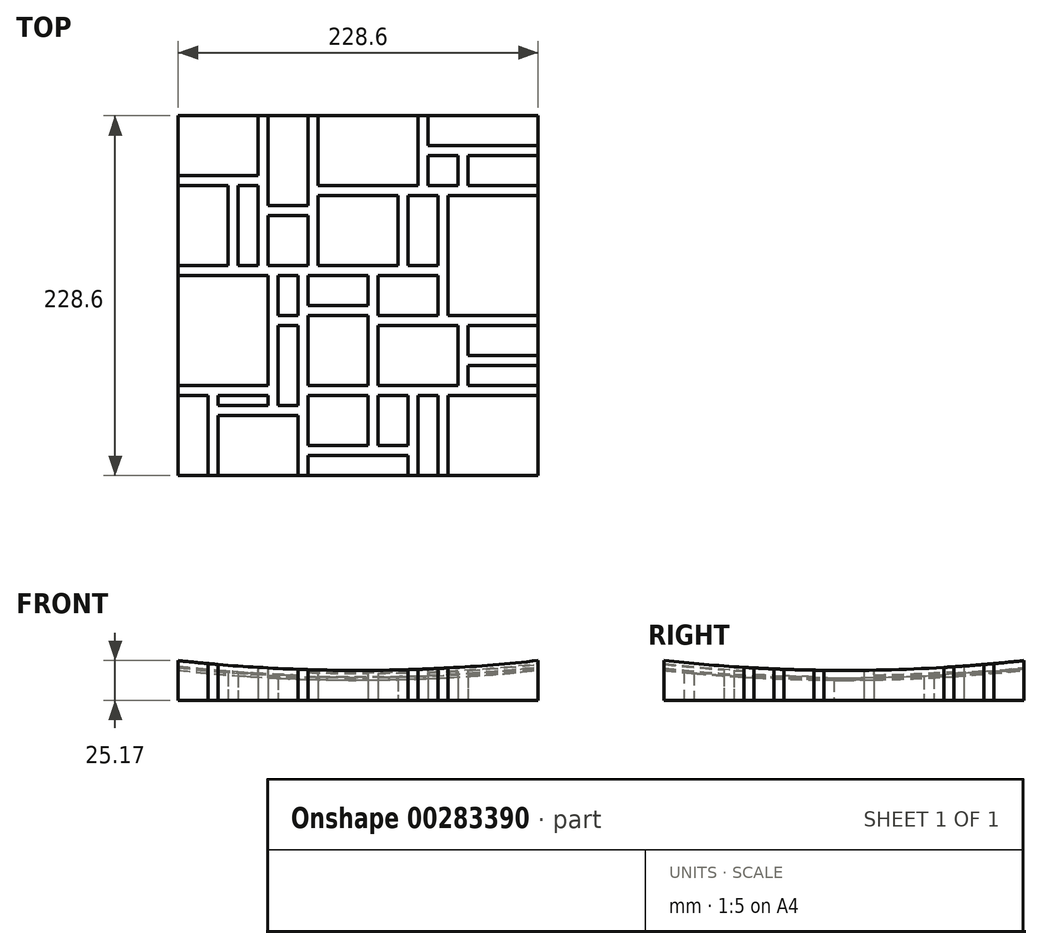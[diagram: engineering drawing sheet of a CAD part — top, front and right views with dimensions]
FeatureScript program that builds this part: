
annotation { "Feature Type Name" : "Feature", "Feature Type Description" : "" }
export const myFeature = defineFeature(function(context is Context, id is Id, definition is map)
    precondition{}
    {
        {
            var Q0;
            Q0=qCreatedBy(makeId("Top.planeOp"),FACE);
            var sketch = newSketch(context, id + "F0", { "sketchPlane" : qUnion([Q0])});
            skLineSegment(sketch, "E0.bottom", {"start": v(114.3, -114.3) * mm, "end": v(-114.3, -114.3) * mm});
            skLineSegment(sketch, "E0.top", {"start": v(114.3, 114.3) * mm, "end": v(-114.3, 114.3) * mm});
            skLineSegment(sketch, "E0.left", {"start": v(114.3, -114.3) * mm, "end": v(114.3, 114.3) * mm});
            skLineSegment(sketch, "E0.right", {"start": v(-114.3, -114.3) * mm, "end": v(-114.3, 114.3) * mm});
            skPoint(sketch, "E0.middle", {"position": v(0, 0) * mm});
            skLineSegment(sketch, "E1", {"start": v(-114.3, 114.3) * mm, "end": v(-63.5, 114.3) * mm, "construction": true});
            skLineSegment(sketch, "E2", {"start": v(-63.5, 114.3) * mm, "end": v(-63.5, 76.2) * mm});
            skLineSegment(sketch, "E3", {"start": v(-63.5, 76.2) * mm, "end": v(-114.3, 76.2) * mm});
            skLineSegment(sketch, "E4", {"start": v(-114.3, 76.2) * mm, "end": v(-114.3, 69.85) * mm, "construction": true});
            skLineSegment(sketch, "E5", {"start": v(-114.3, 69.85) * mm, "end": v(-114.3, 19.05) * mm, "construction": true});
            skLineSegment(sketch, "E6", {"start": v(-114.3, 19.05) * mm, "end": v(-82.55, 19.05) * mm});
            skLineSegment(sketch, "E7", {"start": v(-82.55, 19.05) * mm, "end": v(-82.55, 69.85) * mm});
            skLineSegment(sketch, "E8", {"start": v(-82.55, 69.85) * mm, "end": v(-114.3, 69.85) * mm});
            skLineSegment(sketch, "E9", {"start": v(-82.55, 69.85) * mm, "end": v(-76.2, 69.85) * mm, "construction": true});
            skLineSegment(sketch, "E10", {"start": v(-76.2, 69.85) * mm, "end": v(-63.5, 69.85) * mm});
            skLineSegment(sketch, "E11", {"start": v(-63.5, 69.85) * mm, "end": v(-63.5, 19.05) * mm});
            skLineSegment(sketch, "E12", {"start": v(-63.5, 19.05) * mm, "end": v(-76.2, 19.05) * mm});
            skLineSegment(sketch, "E13", {"start": v(-76.2, 19.05) * mm, "end": v(-76.2, 69.85) * mm});
            skLineSegment(sketch, "E14", {"start": v(-63.5, 114.3) * mm, "end": v(-57.15, 114.3) * mm, "construction": true});
            skLineSegment(sketch, "E15", {"start": v(-57.15, 114.3) * mm, "end": v(-57.15, 57.15) * mm});
            skLineSegment(sketch, "E16", {"start": v(-57.15, 57.15) * mm, "end": v(-31.75, 57.15) * mm});
            skLineSegment(sketch, "E17", {"start": v(-31.75, 57.15) * mm, "end": v(-31.75, 114.3) * mm});
            skLineSegment(sketch, "E18", {"start": v(-31.75, 114.3) * mm, "end": v(-25.4, 114.3) * mm, "construction": true});
            skLineSegment(sketch, "E19", {"start": v(-25.4, 114.3) * mm, "end": v(-25.4, 69.85) * mm});
            skLineSegment(sketch, "E20", {"start": v(-25.4, 69.85) * mm, "end": v(38.1, 69.85) * mm});
            skLineSegment(sketch, "E21", {"start": v(38.1, 69.85) * mm, "end": v(38.1, 114.3) * mm});
            skLineSegment(sketch, "E22", {"start": v(38.1, 114.3) * mm, "end": v(44.45, 114.3) * mm, "construction": true});
            skLineSegment(sketch, "E23", {"start": v(44.45, 114.3) * mm, "end": v(44.45, 95.25) * mm});
            skLineSegment(sketch, "E24", {"start": v(44.45, 95.25) * mm, "end": v(114.3, 95.25) * mm});
            skLineSegment(sketch, "E25", {"start": v(114.3, 95.25) * mm, "end": v(114.3, 88.9) * mm, "construction": true});
            skLineSegment(sketch, "E26", {"start": v(114.3, 88.9) * mm, "end": v(69.85, 88.9) * mm});
            skLineSegment(sketch, "E27", {"start": v(69.85, 88.9) * mm, "end": v(69.85, 69.85) * mm});
            skLineSegment(sketch, "E28", {"start": v(69.85, 69.85) * mm, "end": v(114.3, 69.85) * mm});
            skLineSegment(sketch, "E29", {"start": v(69.85, 88.9) * mm, "end": v(63.5, 88.9) * mm, "construction": true});
            skLineSegment(sketch, "E30", {"start": v(63.5, 88.9) * mm, "end": v(44.45, 88.9) * mm});
            skLineSegment(sketch, "E31", {"start": v(44.45, 88.9) * mm, "end": v(44.45, 69.85) * mm});
            skLineSegment(sketch, "E32", {"start": v(44.45, 69.85) * mm, "end": v(63.5, 69.85) * mm});
            skLineSegment(sketch, "E33", {"start": v(63.5, 69.85) * mm, "end": v(63.5, 88.9) * mm});
            skLineSegment(sketch, "E34", {"start": v(114.3, 69.85) * mm, "end": v(114.3, 63.5) * mm, "construction": true});
            skLineSegment(sketch, "E35", {"start": v(114.3, 63.5) * mm, "end": v(57.15, 63.5) * mm});
            skLineSegment(sketch, "E36", {"start": v(57.15, 63.5) * mm, "end": v(57.15, -12.7) * mm});
            skLineSegment(sketch, "E37", {"start": v(57.15, -12.7) * mm, "end": v(114.3, -12.7) * mm});
            skLineSegment(sketch, "E38", {"start": v(114.3, -12.7) * mm, "end": v(114.3, -19.05) * mm, "construction": true});
            skLineSegment(sketch, "E39", {"start": v(114.3, -19.05) * mm, "end": v(69.85, -19.05) * mm});
            skLineSegment(sketch, "E40", {"start": v(69.85, -19.05) * mm, "end": v(69.85, -38.1) * mm});
            skLineSegment(sketch, "E41", {"start": v(69.85, -38.1) * mm, "end": v(114.3, -38.1) * mm});
            skLineSegment(sketch, "E42", {"start": v(114.3, -38.1) * mm, "end": v(114.3, -44.45) * mm, "construction": true});
            skLineSegment(sketch, "E43", {"start": v(114.3, -44.45) * mm, "end": v(69.85, -44.45) * mm});
            skLineSegment(sketch, "E44", {"start": v(69.85, -44.45) * mm, "end": v(69.85, -57.15) * mm});
            skLineSegment(sketch, "E45", {"start": v(69.85, -57.15) * mm, "end": v(114.3, -57.15) * mm});
            skLineSegment(sketch, "E46", {"start": v(114.3, -57.15) * mm, "end": v(114.3, -63.5) * mm, "construction": true});
            skLineSegment(sketch, "E47", {"start": v(114.3, -63.5) * mm, "end": v(57.15, -63.5) * mm});
            skLineSegment(sketch, "E48", {"start": v(57.15, -63.5) * mm, "end": v(57.15, -114.3) * mm});
            skLineSegment(sketch, "E49", {"start": v(57.15, -114.3) * mm, "end": v(50.8, -114.3) * mm, "construction": true});
            skLineSegment(sketch, "E50", {"start": v(50.8, -114.3) * mm, "end": v(50.8, -63.5) * mm});
            skLineSegment(sketch, "E51", {"start": v(50.8, -63.5) * mm, "end": v(38.1, -63.5) * mm});
            skLineSegment(sketch, "E52", {"start": v(38.1, -63.5) * mm, "end": v(38.1, -114.3) * mm});
            skLineSegment(sketch, "E53", {"start": v(38.1, -114.3) * mm, "end": v(31.75, -114.3) * mm, "construction": true});
            skLineSegment(sketch, "E54", {"start": v(31.75, -114.3) * mm, "end": v(31.75, -101.6) * mm});
            skLineSegment(sketch, "E55", {"start": v(31.75, -101.6) * mm, "end": v(-31.75, -101.6) * mm});
            skLineSegment(sketch, "E56", {"start": v(-31.75, -101.6) * mm, "end": v(-31.75, -114.3) * mm});
            skLineSegment(sketch, "E57", {"start": v(31.75, -101.6) * mm, "end": v(31.75, -95.25) * mm, "construction": true});
            skLineSegment(sketch, "E58", {"start": v(31.75, -95.25) * mm, "end": v(31.75, -63.5) * mm});
            skLineSegment(sketch, "E59", {"start": v(31.75, -63.5) * mm, "end": v(12.7, -63.5) * mm});
            skLineSegment(sketch, "E60", {"start": v(12.7, -63.5) * mm, "end": v(12.7, -95.25) * mm});
            skLineSegment(sketch, "E61", {"start": v(12.7, -95.25) * mm, "end": v(31.75, -95.25) * mm});
            skLineSegment(sketch, "E62", {"start": v(12.7, -63.5) * mm, "end": v(6.35, -63.5) * mm, "construction": true});
            skLineSegment(sketch, "E63", {"start": v(6.35, -63.5) * mm, "end": v(-31.75, -63.5) * mm});
            skLineSegment(sketch, "E64", {"start": v(-31.75, -63.5) * mm, "end": v(-31.75, -95.25) * mm});
            skLineSegment(sketch, "E65", {"start": v(-31.75, -95.25) * mm, "end": v(6.35, -95.25) * mm});
            skLineSegment(sketch, "E66", {"start": v(6.35, -95.25) * mm, "end": v(6.35, -63.5) * mm});
            skLineSegment(sketch, "E67", {"start": v(12.7, -63.5) * mm, "end": v(12.7, -57.15) * mm, "construction": true});
            skLineSegment(sketch, "E68", {"start": v(12.7, -57.15) * mm, "end": v(63.5, -57.15) * mm});
            skLineSegment(sketch, "E69", {"start": v(63.5, -57.15) * mm, "end": v(63.5, -19.05) * mm});
            skLineSegment(sketch, "E70", {"start": v(63.5, -19.05) * mm, "end": v(12.7, -19.05) * mm});
            skLineSegment(sketch, "E71", {"start": v(12.7, -19.05) * mm, "end": v(12.7, -57.15) * mm});
            skLineSegment(sketch, "E72", {"start": v(-31.75, -114.3) * mm, "end": v(-38.1, -114.3) * mm, "construction": true});
            skLineSegment(sketch, "E73", {"start": v(-38.1, -114.3) * mm, "end": v(-38.1, -76.2) * mm});
            skLineSegment(sketch, "E74", {"start": v(-38.1, -76.2) * mm, "end": v(-88.9, -76.2) * mm});
            skLineSegment(sketch, "E75", {"start": v(-88.9, -76.2) * mm, "end": v(-88.9, -114.3) * mm});
            skLineSegment(sketch, "E76", {"start": v(-88.9, -114.3) * mm, "end": v(-95.25, -114.3) * mm, "construction": true});
            skLineSegment(sketch, "E77", {"start": v(-95.25, -114.3) * mm, "end": v(-95.25, -63.5) * mm});
            skLineSegment(sketch, "E78", {"start": v(-95.25, -63.5) * mm, "end": v(-114.3, -63.5) * mm});
            skLineSegment(sketch, "E79", {"start": v(-114.3, -63.5) * mm, "end": v(-114.3, -57.15) * mm, "construction": true});
            skLineSegment(sketch, "E80", {"start": v(-114.3, -57.15) * mm, "end": v(-57.15, -57.15) * mm});
            skLineSegment(sketch, "E81", {"start": v(-57.15, -57.15) * mm, "end": v(-57.15, 12.7) * mm});
            skLineSegment(sketch, "E82", {"start": v(-57.15, 12.7) * mm, "end": v(-114.3, 12.7) * mm});
            skLineSegment(sketch, "E83", {"start": v(-88.9, -76.2) * mm, "end": v(-88.9, -69.85) * mm, "construction": true});
            skLineSegment(sketch, "E84", {"start": v(-88.9, -69.85) * mm, "end": v(-88.9, -63.5) * mm});
            skLineSegment(sketch, "E85", {"start": v(-88.9, -63.5) * mm, "end": v(-57.15, -63.5) * mm});
            skLineSegment(sketch, "E86", {"start": v(-57.15, -63.5) * mm, "end": v(-57.15, -69.85) * mm});
            skLineSegment(sketch, "E87", {"start": v(-57.15, -69.85) * mm, "end": v(-88.9, -69.85) * mm});
            skLineSegment(sketch, "E88", {"start": v(-38.1, -76.2) * mm, "end": v(-38.1, -69.85) * mm, "construction": true});
            skLineSegment(sketch, "E89", {"start": v(-38.1, -69.85) * mm, "end": v(-50.8, -69.85) * mm});
            skLineSegment(sketch, "E90", {"start": v(-50.8, -69.85) * mm, "end": v(-50.8, -19.05) * mm});
            skLineSegment(sketch, "E91", {"start": v(-50.8, -19.05) * mm, "end": v(-38.1, -19.05) * mm});
            skLineSegment(sketch, "E92", {"start": v(-38.1, -19.05) * mm, "end": v(-38.1, -69.85) * mm});
            skLineSegment(sketch, "E93", {"start": v(-63.5, 19.05) * mm, "end": v(-57.15, 19.05) * mm, "construction": true});
            skLineSegment(sketch, "E94", {"start": v(-57.15, 19.05) * mm, "end": v(-57.15, 50.8) * mm});
            skLineSegment(sketch, "E95", {"start": v(-57.15, 50.8) * mm, "end": v(-31.75, 50.8) * mm});
            skLineSegment(sketch, "E96", {"start": v(-31.75, 50.8) * mm, "end": v(-31.75, 19.05) * mm});
            skLineSegment(sketch, "E97", {"start": v(-31.75, 19.05) * mm, "end": v(-57.15, 19.05) * mm});
            skLineSegment(sketch, "E98", {"start": v(-38.1, -19.05) * mm, "end": v(-38.1, -12.7) * mm, "construction": true});
            skLineSegment(sketch, "E99", {"start": v(-38.1, -12.7) * mm, "end": v(-50.8, -12.7) * mm});
            skLineSegment(sketch, "E100", {"start": v(-50.8, -12.7) * mm, "end": v(-50.8, 12.7) * mm});
            skLineSegment(sketch, "E101", {"start": v(-50.8, 12.7) * mm, "end": v(-38.1, 12.7) * mm});
            skLineSegment(sketch, "E102", {"start": v(-38.1, 12.7) * mm, "end": v(-38.1, -12.7) * mm});
            skLineSegment(sketch, "E103", {"start": v(-31.75, -63.5) * mm, "end": v(-31.75, -57.15) * mm, "construction": true});
            skLineSegment(sketch, "E104", {"start": v(-31.75, -57.15) * mm, "end": v(-31.75, -12.7) * mm});
            skLineSegment(sketch, "E105", {"start": v(-31.75, -12.7) * mm, "end": v(6.35, -12.7) * mm});
            skLineSegment(sketch, "E106", {"start": v(6.35, -12.7) * mm, "end": v(6.35, -57.15) * mm});
            skLineSegment(sketch, "E107", {"start": v(6.35, -57.15) * mm, "end": v(-31.75, -57.15) * mm});
            skLineSegment(sketch, "E108", {"start": v(-31.75, 19.05) * mm, "end": v(-31.75, 12.7) * mm, "construction": true});
            skLineSegment(sketch, "E109", {"start": v(-31.75, 12.7) * mm, "end": v(-31.75, -6.35) * mm});
            skLineSegment(sketch, "E110", {"start": v(-31.75, -6.35) * mm, "end": v(6.35, -6.35) * mm});
            skLineSegment(sketch, "E111", {"start": v(6.35, -6.35) * mm, "end": v(6.35, 12.7) * mm});
            skLineSegment(sketch, "E112", {"start": v(6.35, 12.7) * mm, "end": v(-31.75, 12.7) * mm});
            skLineSegment(sketch, "E113", {"start": v(-25.4, 69.85) * mm, "end": v(-25.4, 63.5) * mm, "construction": true});
            skLineSegment(sketch, "E114", {"start": v(-25.4, 63.5) * mm, "end": v(-25.4, 19.05) * mm});
            skLineSegment(sketch, "E115", {"start": v(-25.4, 19.05) * mm, "end": v(25.4, 19.05) * mm});
            skLineSegment(sketch, "E116", {"start": v(25.4, 19.05) * mm, "end": v(25.4, 63.5) * mm});
            skLineSegment(sketch, "E117", {"start": v(25.4, 63.5) * mm, "end": v(-25.4, 63.5) * mm});
            skLineSegment(sketch, "E118", {"start": v(25.4, 63.5) * mm, "end": v(31.75, 63.5) * mm, "construction": true});
            skLineSegment(sketch, "E119", {"start": v(31.75, 63.5) * mm, "end": v(31.75, 19.05) * mm});
            skLineSegment(sketch, "E120", {"start": v(31.75, 19.05) * mm, "end": v(50.8, 19.05) * mm});
            skLineSegment(sketch, "E121", {"start": v(50.8, 19.05) * mm, "end": v(50.8, 63.5) * mm});
            skLineSegment(sketch, "E122", {"start": v(50.8, 63.5) * mm, "end": v(31.75, 63.5) * mm});
            skLineSegment(sketch, "E123", {"start": v(50.8, 19.05) * mm, "end": v(50.8, 12.7) * mm, "construction": true});
            skLineSegment(sketch, "E124", {"start": v(50.8, 12.7) * mm, "end": v(12.7, 12.7) * mm});
            skLineSegment(sketch, "E125", {"start": v(12.7, 12.7) * mm, "end": v(12.7, -12.7) * mm});
            skLineSegment(sketch, "E126", {"start": v(12.7, -12.7) * mm, "end": v(50.8, -12.7) * mm});
            skLineSegment(sketch, "E127", {"start": v(50.8, -12.7) * mm, "end": v(50.8, 12.7) * mm});
            skSolve(sketch);
        }
        {
            var Q0;
            {var subQ15=sQuery(id+"F0.wireOp",EDGE,"E2");Q0=makeQuery(id+"F0.imprint","IMPRINT",FACE,{"disambiguationData":[TD([[makeQuery(id+"F0.imprint","IMPRINT",EDGE,{"derivedFrom":subQ15}),1.0]])]});}
            extrude(context, id + "F1", {"entities" : qUnion([Q0]), "depth" : 25.4 * mm});
        }
        {
            var Q0;
            {var subQ0=sQuery(id+"F0.wireOp",EDGE,"E73");Q0=makeQuery(id+"F0.imprint","IMPRINT",FACE,{"disambiguationData":[TD([[makeQuery(id+"F0.imprint","IMPRINT",EDGE,{"derivedFrom":subQ0}),1.0]])]});}
            var Q1;
            Q1=makeQuery(id+"F0.imprint","IMPRINT",FACE,{"disambiguationData":[TD([[makeQuery(id+"F0.imprint","IMPRINT",EDGE,{"derivedFrom":sQuery(id+"F0.wireOp",EDGE,"E114")}),1.0]])]});
            var Q2;
            Q2=makeQuery(id+"F0.imprint","IMPRINT",FACE,{"disambiguationData":[TD([[makeQuery(id+"F0.imprint","IMPRINT",EDGE,{"derivedFrom":sQuery(id+"F0.wireOp",EDGE,"E68")}),1.0]])]});
            var Q3;
            {var subQ0=sQuery(id+"F0.wireOp",EDGE,"E80");Q3=makeQuery(id+"F0.imprint","IMPRINT",FACE,{"disambiguationData":[TD([[makeQuery(id+"F0.imprint","IMPRINT",EDGE,{"derivedFrom":subQ0}),1.0]])]});}
            var Q4;
            Q4=makeQuery(id+"F0.imprint","IMPRINT",FACE,{"disambiguationData":[TD([[makeQuery(id+"F0.imprint","IMPRINT",EDGE,{"derivedFrom":sQuery(id+"F0.wireOp",EDGE,"E89")}),-1.0]])]});
            var Q5;
            Q5=makeQuery(id+"F0.imprint","IMPRINT",FACE,{"disambiguationData":[TD([[makeQuery(id+"F0.imprint","IMPRINT",EDGE,{"derivedFrom":sQuery(id+"F0.wireOp",EDGE,"E84")}),-1.0]])]});
            var Q6;
            {var subQ3=sQuery(id+"F0.wireOp",EDGE,"E77");Q6=makeQuery(id+"F0.imprint","IMPRINT",FACE,{"disambiguationData":[TD([[makeQuery(id+"F0.imprint","IMPRINT",EDGE,{"derivedFrom":subQ3}),1.0]])]});}
            var Q7;
            Q7=makeQuery(id+"F0.imprint","IMPRINT",FACE,{"disambiguationData":[TD([[makeQuery(id+"F0.imprint","IMPRINT",EDGE,{"derivedFrom":sQuery(id+"F0.wireOp",EDGE,"E63")}),1.0]])]});
            var Q8;
            Q8=makeQuery(id+"F0.imprint","IMPRINT",FACE,{"disambiguationData":[TD([[makeQuery(id+"F0.imprint","IMPRINT",EDGE,{"derivedFrom":sQuery(id+"F0.wireOp",EDGE,"E104")}),-1.0]])]});
            var Q9;
            {var subQ0=sQuery(id+"F0.wireOp",EDGE,"E54");Q9=makeQuery(id+"F0.imprint","IMPRINT",FACE,{"disambiguationData":[TD([[makeQuery(id+"F0.imprint","IMPRINT",EDGE,{"derivedFrom":subQ0}),1.0]])]});}
            var Q10;
            Q10=makeQuery(id+"F0.imprint","IMPRINT",FACE,{"disambiguationData":[TD([[makeQuery(id+"F0.imprint","IMPRINT",EDGE,{"derivedFrom":sQuery(id+"F0.wireOp",EDGE,"E58")}),1.0]])]});
            var Q11;
            {var subQ0=sQuery(id+"F0.wireOp",EDGE,"E50");Q11=makeQuery(id+"F0.imprint","IMPRINT",FACE,{"disambiguationData":[TD([[makeQuery(id+"F0.imprint","IMPRINT",EDGE,{"derivedFrom":subQ0}),1.0]])]});}
            var Q12;
            {var subQ4=sQuery(id+"F0.wireOp",EDGE,"E47");Q12=makeQuery(id+"F0.imprint","IMPRINT",FACE,{"disambiguationData":[TD([[makeQuery(id+"F0.imprint","IMPRINT",EDGE,{"derivedFrom":subQ4}),1.0]])]});}
            var Q13;
            {var subQ0=sQuery(id+"F0.wireOp",EDGE,"E43");Q13=makeQuery(id+"F0.imprint","IMPRINT",FACE,{"disambiguationData":[TD([[makeQuery(id+"F0.imprint","IMPRINT",EDGE,{"derivedFrom":subQ0}),1.0]])]});}
            var Q14;
            {var subQ0=sQuery(id+"F0.wireOp",EDGE,"E39");Q14=makeQuery(id+"F0.imprint","IMPRINT",FACE,{"disambiguationData":[TD([[makeQuery(id+"F0.imprint","IMPRINT",EDGE,{"derivedFrom":subQ0}),1.0]])]});}
            var Q15;
            {var subQ0=sQuery(id+"F0.wireOp",EDGE,"E35");Q15=makeQuery(id+"F0.imprint","IMPRINT",FACE,{"disambiguationData":[TD([[makeQuery(id+"F0.imprint","IMPRINT",EDGE,{"derivedFrom":subQ0}),1.0]])]});}
            var Q16;
            {var subQ0=sQuery(id+"F0.wireOp",EDGE,"E26");Q16=makeQuery(id+"F0.imprint","IMPRINT",FACE,{"disambiguationData":[TD([[makeQuery(id+"F0.imprint","IMPRINT",EDGE,{"derivedFrom":subQ0}),1.0]])]});}
            var Q17;
            Q17=makeQuery(id+"F0.imprint","IMPRINT",FACE,{"disambiguationData":[TD([[makeQuery(id+"F0.imprint","IMPRINT",EDGE,{"derivedFrom":sQuery(id+"F0.wireOp",EDGE,"E30")}),1.0]])]});
            var Q18;
            {var subQ3=sQuery(id+"F0.wireOp",EDGE,"E23");Q18=makeQuery(id+"F0.imprint","IMPRINT",FACE,{"disambiguationData":[TD([[makeQuery(id+"F0.imprint","IMPRINT",EDGE,{"derivedFrom":subQ3}),1.0]])]});}
            var Q19;
            {var subQ0=sQuery(id+"F0.wireOp",EDGE,"E19");Q19=makeQuery(id+"F0.imprint","IMPRINT",FACE,{"disambiguationData":[TD([[makeQuery(id+"F0.imprint","IMPRINT",EDGE,{"derivedFrom":subQ0}),1.0]])]});}
            var Q20;
            Q20=makeQuery(id+"F0.imprint","IMPRINT",FACE,{"disambiguationData":[TD([[makeQuery(id+"F0.imprint","IMPRINT",EDGE,{"derivedFrom":sQuery(id+"F0.wireOp",EDGE,"E119")}),1.0]])]});
            var Q21;
            Q21=makeQuery(id+"F0.imprint","IMPRINT",FACE,{"disambiguationData":[TD([[makeQuery(id+"F0.imprint","IMPRINT",EDGE,{"derivedFrom":sQuery(id+"F0.wireOp",EDGE,"E124")}),1.0]])]});
            var Q22;
            Q22=makeQuery(id+"F0.imprint","IMPRINT",FACE,{"disambiguationData":[TD([[makeQuery(id+"F0.imprint","IMPRINT",EDGE,{"derivedFrom":sQuery(id+"F0.wireOp",EDGE,"E109")}),1.0]])]});
            var Q23;
            Q23=makeQuery(id+"F0.imprint","IMPRINT",FACE,{"disambiguationData":[TD([[makeQuery(id+"F0.imprint","IMPRINT",EDGE,{"derivedFrom":sQuery(id+"F0.wireOp",EDGE,"E99")}),-1.0]])]});
            var Q24;
            Q24=makeQuery(id+"F0.imprint","IMPRINT",FACE,{"disambiguationData":[TD([[makeQuery(id+"F0.imprint","IMPRINT",EDGE,{"derivedFrom":sQuery(id+"F0.wireOp",EDGE,"E94")}),-1.0]])]});
            var Q25;
            Q25=makeQuery(id+"F0.imprint","IMPRINT",FACE,{"disambiguationData":[TD([[makeQuery(id+"F0.imprint","IMPRINT",EDGE,{"derivedFrom":sQuery(id+"F0.wireOp",EDGE,"E10")}),-1.0]])]});
            var Q26;
            {var subQ0=sQuery(id+"F0.wireOp",EDGE,"E6");Q26=makeQuery(id+"F0.imprint","IMPRINT",FACE,{"disambiguationData":[TD([[makeQuery(id+"F0.imprint","IMPRINT",EDGE,{"derivedFrom":subQ0}),1.0]])]});}
            var Q27;
            {var subQ3=sQuery(id+"F0.wireOp",EDGE,"E2");Q27=makeQuery(id+"F0.imprint","IMPRINT",FACE,{"disambiguationData":[TD([[makeQuery(id+"F0.imprint","IMPRINT",EDGE,{"derivedFrom":subQ3}),-1.0]])]});}
            var Q28;
            {var subQ0=sQuery(id+"F0.wireOp",EDGE,"E15");Q28=makeQuery(id+"F0.imprint","IMPRINT",FACE,{"disambiguationData":[TD([[makeQuery(id+"F0.imprint","IMPRINT",EDGE,{"derivedFrom":subQ0}),1.0]])]});}
            extrude(context, id + "F2", {"entities" : qUnion([Q0, Q1, Q2, Q3, Q4, Q5, Q6, Q7, Q8, Q9, Q10, Q11, Q12, Q13, Q14, Q15, Q16, Q17, Q18, Q19, Q20, Q21, Q22, Q23, Q24, Q25, Q26, Q27, Q28]), "depth" : 25.4 * mm});
        }
        {
            var Q0;
            Q0=qCreatedBy(makeId("Front.planeOp"),FACE);
            var sketch = newSketch(context, id + "F3", { "sketchPlane" : qUnion([Q0])});
            skLineSegment(sketch, "E128", {"start": v(0, 0) * mm, "end": v(0, 1066.8) * mm, "construction": true});
            skCircle(sketch, "E129", {"center": v(0, 1066.8) * mm, "radius": 1054.1 * mm});
            skLineSegment(sketch, "E130", {"start": v(0, 0) * mm, "end": v(0, 2540) * mm});
            skSolve(sketch);
        }
        {
            var Q0;
            {var subQ0=sQuery(id+"F3.wireOp",EDGE,"E130");var subQ1=sQuery(id+"F3.wireOp",EDGE,"E129");var subQ2=makeQuery(id+"F3.imprint","INTERSECT",VERTEX,{"disambiguationData":[OD(0.0)],"derivedFrom":[subQ1,subQ0]});Q0=makeQuery(id+"F3.imprint","IMPRINT",FACE,{"disambiguationData":[TD([[makeQuery(id+"F3.imprint","IMPRINT",EDGE,{"disambiguationData":[TD([[subQ2,-1.0]])],"derivedFrom":subQ1}),1.0]])]});}
            var Q1;
            Q1=sQuery(id+"F3.wireOp",EDGE,"E129");
            var Q2;
            Q2=sQuery(id+"F3.wireOp",EDGE,"E130");
            revolve(context, id + "F4", {"entities" : qUnion([Q0]), "surfaceEntities" : qUnion([Q1]), "axis" : qUnion([Q2]), "revolveType" : RevolveType.FULL});
        }
        {
            var Q0;
            Q0=makeQuery(id+"F4.opRevolve","SWEPT_BODY",BODY,{"disambiguationData":[OSD([sQuery(id+"F3.wireOp",EDGE,"E129"),sQuery(id+"F3.wireOp",EDGE,"E130")])]});
            var Q1;
            Q1=makeQuery(id+"F2.opExtrude","SWEPT_BODY",BODY,{"disambiguationData":[OSD([sQuery(id+"F0.wireOp",EDGE,"E0.top"),sQuery(id+"F0.wireOp",EDGE,"E0.right"),sQuery(id+"F0.wireOp",EDGE,"E2"),sQuery(id+"F0.wireOp",EDGE,"E3")])]});
            var Q2;
            Q2=makeQuery(id+"F2.opExtrude","SWEPT_BODY",BODY,{"disambiguationData":[OSD([sQuery(id+"F0.wireOp",EDGE,"E0.top"),sQuery(id+"F0.wireOp",EDGE,"E19"),sQuery(id+"F0.wireOp",EDGE,"E20"),sQuery(id+"F0.wireOp",EDGE,"E21")])]});
            var Q3;
            Q3=makeQuery(id+"F2.opExtrude","SWEPT_BODY",BODY,{"disambiguationData":[OSD([sQuery(id+"F0.wireOp",EDGE,"E0.top"),sQuery(id+"F0.wireOp",EDGE,"E0.left"),sQuery(id+"F0.wireOp",EDGE,"E23"),sQuery(id+"F0.wireOp",EDGE,"E24")])]});
            var Q4;
            Q4=makeQuery(id+"F2.opExtrude","SWEPT_BODY",BODY,{"disambiguationData":[OSD([sQuery(id+"F0.wireOp",EDGE,"E0.top"),sQuery(id+"F0.wireOp",EDGE,"E15"),sQuery(id+"F0.wireOp",EDGE,"E16"),sQuery(id+"F0.wireOp",EDGE,"E17")])]});
            var Q5;
            Q5=makeQuery(id+"F2.opExtrude","SWEPT_BODY",BODY,{"disambiguationData":[OSD([sQuery(id+"F0.wireOp",EDGE,"E0.bottom"),sQuery(id+"F0.wireOp",EDGE,"E0.right"),sQuery(id+"F0.wireOp",EDGE,"E77"),sQuery(id+"F0.wireOp",EDGE,"E78")])]});
            var Q6;
            Q6=makeQuery(id+"F2.opExtrude","SWEPT_BODY",BODY,{"disambiguationData":[OSD([sQuery(id+"F0.wireOp",EDGE,"E0.bottom"),sQuery(id+"F0.wireOp",EDGE,"E0.left"),sQuery(id+"F0.wireOp",EDGE,"E47"),sQuery(id+"F0.wireOp",EDGE,"E48")])]});
            var Q7;
            Q7=makeQuery(id+"F1.opExtrude","SWEPT_BODY",BODY,{"disambiguationData":[OSD([sQuery(id+"F0.wireOp",EDGE,"E0.bottom"),sQuery(id+"F0.wireOp",EDGE,"E0.top"),sQuery(id+"F0.wireOp",EDGE,"E0.left"),sQuery(id+"F0.wireOp",EDGE,"E0.right"),sQuery(id+"F0.wireOp",EDGE,"E2"),sQuery(id+"F0.wireOp",EDGE,"E3"),sQuery(id+"F0.wireOp",EDGE,"E6"),sQuery(id+"F0.wireOp",EDGE,"E7"),sQuery(id+"F0.wireOp",EDGE,"E8"),sQuery(id+"F0.wireOp",EDGE,"E10"),sQuery(id+"F0.wireOp",EDGE,"E11"),sQuery(id+"F0.wireOp",EDGE,"E12"),sQuery(id+"F0.wireOp",EDGE,"E13"),sQuery(id+"F0.wireOp",EDGE,"E15"),sQuery(id+"F0.wireOp",EDGE,"E16"),sQuery(id+"F0.wireOp",EDGE,"E17"),sQuery(id+"F0.wireOp",EDGE,"E19"),sQuery(id+"F0.wireOp",EDGE,"E20"),sQuery(id+"F0.wireOp",EDGE,"E21"),sQuery(id+"F0.wireOp",EDGE,"E23"),sQuery(id+"F0.wireOp",EDGE,"E24"),sQuery(id+"F0.wireOp",EDGE,"E26"),sQuery(id+"F0.wireOp",EDGE,"E27"),sQuery(id+"F0.wireOp",EDGE,"E28"),sQuery(id+"F0.wireOp",EDGE,"E30"),sQuery(id+"F0.wireOp",EDGE,"E31"),sQuery(id+"F0.wireOp",EDGE,"E32"),sQuery(id+"F0.wireOp",EDGE,"E33"),sQuery(id+"F0.wireOp",EDGE,"E35"),sQuery(id+"F0.wireOp",EDGE,"E36"),sQuery(id+"F0.wireOp",EDGE,"E37"),sQuery(id+"F0.wireOp",EDGE,"E39"),sQuery(id+"F0.wireOp",EDGE,"E40"),sQuery(id+"F0.wireOp",EDGE,"E41"),sQuery(id+"F0.wireOp",EDGE,"E43"),sQuery(id+"F0.wireOp",EDGE,"E44"),sQuery(id+"F0.wireOp",EDGE,"E45"),sQuery(id+"F0.wireOp",EDGE,"E47"),sQuery(id+"F0.wireOp",EDGE,"E48"),sQuery(id+"F0.wireOp",EDGE,"E50"),sQuery(id+"F0.wireOp",EDGE,"E51"),sQuery(id+"F0.wireOp",EDGE,"E52"),sQuery(id+"F0.wireOp",EDGE,"E54"),sQuery(id+"F0.wireOp",EDGE,"E55"),sQuery(id+"F0.wireOp",EDGE,"E56"),sQuery(id+"F0.wireOp",EDGE,"E58"),sQuery(id+"F0.wireOp",EDGE,"E59"),sQuery(id+"F0.wireOp",EDGE,"E60"),sQuery(id+"F0.wireOp",EDGE,"E61"),sQuery(id+"F0.wireOp",EDGE,"E63"),sQuery(id+"F0.wireOp",EDGE,"E64"),sQuery(id+"F0.wireOp",EDGE,"E65"),sQuery(id+"F0.wireOp",EDGE,"E66"),sQuery(id+"F0.wireOp",EDGE,"E68"),sQuery(id+"F0.wireOp",EDGE,"E69"),sQuery(id+"F0.wireOp",EDGE,"E70"),sQuery(id+"F0.wireOp",EDGE,"E71"),sQuery(id+"F0.wireOp",EDGE,"E73"),sQuery(id+"F0.wireOp",EDGE,"E74"),sQuery(id+"F0.wireOp",EDGE,"E75"),sQuery(id+"F0.wireOp",EDGE,"E77"),sQuery(id+"F0.wireOp",EDGE,"E78"),sQuery(id+"F0.wireOp",EDGE,"E80"),sQuery(id+"F0.wireOp",EDGE,"E81"),sQuery(id+"F0.wireOp",EDGE,"E82"),sQuery(id+"F0.wireOp",EDGE,"E84"),sQuery(id+"F0.wireOp",EDGE,"E85"),sQuery(id+"F0.wireOp",EDGE,"E86"),sQuery(id+"F0.wireOp",EDGE,"E87"),sQuery(id+"F0.wireOp",EDGE,"E89"),sQuery(id+"F0.wireOp",EDGE,"E90"),sQuery(id+"F0.wireOp",EDGE,"E91"),sQuery(id+"F0.wireOp",EDGE,"E92"),sQuery(id+"F0.wireOp",EDGE,"E94"),sQuery(id+"F0.wireOp",EDGE,"E95"),sQuery(id+"F0.wireOp",EDGE,"E96"),sQuery(id+"F0.wireOp",EDGE,"E97"),sQuery(id+"F0.wireOp",EDGE,"E99"),sQuery(id+"F0.wireOp",EDGE,"E100"),sQuery(id+"F0.wireOp",EDGE,"E101"),sQuery(id+"F0.wireOp",EDGE,"E102"),sQuery(id+"F0.wireOp",EDGE,"E104"),sQuery(id+"F0.wireOp",EDGE,"E105"),sQuery(id+"F0.wireOp",EDGE,"E106"),sQuery(id+"F0.wireOp",EDGE,"E107"),sQuery(id+"F0.wireOp",EDGE,"E109"),sQuery(id+"F0.wireOp",EDGE,"E110"),sQuery(id+"F0.wireOp",EDGE,"E111"),sQuery(id+"F0.wireOp",EDGE,"E112"),sQuery(id+"F0.wireOp",EDGE,"E114"),sQuery(id+"F0.wireOp",EDGE,"E115"),sQuery(id+"F0.wireOp",EDGE,"E116"),sQuery(id+"F0.wireOp",EDGE,"E117"),sQuery(id+"F0.wireOp",EDGE,"E119"),sQuery(id+"F0.wireOp",EDGE,"E120"),sQuery(id+"F0.wireOp",EDGE,"E121"),sQuery(id+"F0.wireOp",EDGE,"E122"),sQuery(id+"F0.wireOp",EDGE,"E124"),sQuery(id+"F0.wireOp",EDGE,"E125"),sQuery(id+"F0.wireOp",EDGE,"E126"),sQuery(id+"F0.wireOp",EDGE,"E127")])]});
            var Q8;
            Q8=makeQuery(id+"F2.opExtrude","SWEPT_BODY",BODY,{"disambiguationData":[OSD([sQuery(id+"F0.wireOp",EDGE,"E0.bottom"),sQuery(id+"F0.wireOp",EDGE,"E73"),sQuery(id+"F0.wireOp",EDGE,"E74"),sQuery(id+"F0.wireOp",EDGE,"E75")])]});
            var Q9;
            Q9=makeQuery(id+"F2.opExtrude","SWEPT_BODY",BODY,{"disambiguationData":[OSD([sQuery(id+"F0.wireOp",EDGE,"E0.right"),sQuery(id+"F0.wireOp",EDGE,"E80"),sQuery(id+"F0.wireOp",EDGE,"E81"),sQuery(id+"F0.wireOp",EDGE,"E82")])]});
            var Q10;
            Q10=makeQuery(id+"F2.opExtrude","SWEPT_BODY",BODY,{"disambiguationData":[OSD([sQuery(id+"F0.wireOp",EDGE,"E0.right"),sQuery(id+"F0.wireOp",EDGE,"E6"),sQuery(id+"F0.wireOp",EDGE,"E7"),sQuery(id+"F0.wireOp",EDGE,"E8")])]});
            var Q11;
            Q11=makeQuery(id+"F2.opExtrude","SWEPT_BODY",BODY,{"disambiguationData":[OSD([sQuery(id+"F0.wireOp",EDGE,"E89"),sQuery(id+"F0.wireOp",EDGE,"E90"),sQuery(id+"F0.wireOp",EDGE,"E91"),sQuery(id+"F0.wireOp",EDGE,"E92")])]});
            var Q12;
            Q12=makeQuery(id+"F2.opExtrude","SWEPT_BODY",BODY,{"disambiguationData":[OSD([sQuery(id+"F0.wireOp",EDGE,"E0.bottom"),sQuery(id+"F0.wireOp",EDGE,"E54"),sQuery(id+"F0.wireOp",EDGE,"E55"),sQuery(id+"F0.wireOp",EDGE,"E56")])]});
            var Q13;
            Q13=makeQuery(id+"F2.opExtrude","SWEPT_BODY",BODY,{"disambiguationData":[OSD([sQuery(id+"F0.wireOp",EDGE,"E0.bottom"),sQuery(id+"F0.wireOp",EDGE,"E50"),sQuery(id+"F0.wireOp",EDGE,"E51"),sQuery(id+"F0.wireOp",EDGE,"E52")])]});
            var Q14;
            Q14=makeQuery(id+"F2.opExtrude","SWEPT_BODY",BODY,{"disambiguationData":[OSD([sQuery(id+"F0.wireOp",EDGE,"E109"),sQuery(id+"F0.wireOp",EDGE,"E110"),sQuery(id+"F0.wireOp",EDGE,"E111"),sQuery(id+"F0.wireOp",EDGE,"E112")])]});
            var Q15;
            Q15=makeQuery(id+"F2.opExtrude","SWEPT_BODY",BODY,{"disambiguationData":[OSD([sQuery(id+"F0.wireOp",EDGE,"E0.left"),sQuery(id+"F0.wireOp",EDGE,"E43"),sQuery(id+"F0.wireOp",EDGE,"E44"),sQuery(id+"F0.wireOp",EDGE,"E45")])]});
            var Q16;
            Q16=makeQuery(id+"F2.opExtrude","SWEPT_BODY",BODY,{"disambiguationData":[OSD([sQuery(id+"F0.wireOp",EDGE,"E0.left"),sQuery(id+"F0.wireOp",EDGE,"E35"),sQuery(id+"F0.wireOp",EDGE,"E36"),sQuery(id+"F0.wireOp",EDGE,"E37")])]});
            var Q17;
            Q17=makeQuery(id+"F2.opExtrude","SWEPT_BODY",BODY,{"disambiguationData":[OSD([sQuery(id+"F0.wireOp",EDGE,"E0.left"),sQuery(id+"F0.wireOp",EDGE,"E39"),sQuery(id+"F0.wireOp",EDGE,"E40"),sQuery(id+"F0.wireOp",EDGE,"E41")])]});
            var Q18;
            Q18=makeQuery(id+"F2.opExtrude","SWEPT_BODY",BODY,{"disambiguationData":[OSD([sQuery(id+"F0.wireOp",EDGE,"E0.left"),sQuery(id+"F0.wireOp",EDGE,"E26"),sQuery(id+"F0.wireOp",EDGE,"E27"),sQuery(id+"F0.wireOp",EDGE,"E28")])]});
            var Q19;
            Q19=makeQuery(id+"F2.opExtrude","SWEPT_BODY",BODY,{"disambiguationData":[OSD([sQuery(id+"F0.wireOp",EDGE,"E10"),sQuery(id+"F0.wireOp",EDGE,"E11"),sQuery(id+"F0.wireOp",EDGE,"E12"),sQuery(id+"F0.wireOp",EDGE,"E13")])]});
            var Q20;
            Q20=makeQuery(id+"F2.opExtrude","SWEPT_BODY",BODY,{"disambiguationData":[OSD([sQuery(id+"F0.wireOp",EDGE,"E30"),sQuery(id+"F0.wireOp",EDGE,"E31"),sQuery(id+"F0.wireOp",EDGE,"E32"),sQuery(id+"F0.wireOp",EDGE,"E33")])]});
            var Q21;
            Q21=makeQuery(id+"F2.opExtrude","SWEPT_BODY",BODY,{"disambiguationData":[OSD([sQuery(id+"F0.wireOp",EDGE,"E58"),sQuery(id+"F0.wireOp",EDGE,"E59"),sQuery(id+"F0.wireOp",EDGE,"E60"),sQuery(id+"F0.wireOp",EDGE,"E61")])]});
            var Q22;
            Q22=makeQuery(id+"F2.opExtrude","SWEPT_BODY",BODY,{"disambiguationData":[OSD([sQuery(id+"F0.wireOp",EDGE,"E63"),sQuery(id+"F0.wireOp",EDGE,"E64"),sQuery(id+"F0.wireOp",EDGE,"E65"),sQuery(id+"F0.wireOp",EDGE,"E66")])]});
            var Q23;
            Q23=makeQuery(id+"F2.opExtrude","SWEPT_BODY",BODY,{"disambiguationData":[OSD([sQuery(id+"F0.wireOp",EDGE,"E68"),sQuery(id+"F0.wireOp",EDGE,"E69"),sQuery(id+"F0.wireOp",EDGE,"E70"),sQuery(id+"F0.wireOp",EDGE,"E71")])]});
            var Q24;
            Q24=makeQuery(id+"F2.opExtrude","SWEPT_BODY",BODY,{"disambiguationData":[OSD([sQuery(id+"F0.wireOp",EDGE,"E84"),sQuery(id+"F0.wireOp",EDGE,"E85"),sQuery(id+"F0.wireOp",EDGE,"E86"),sQuery(id+"F0.wireOp",EDGE,"E87")])]});
            var Q25;
            Q25=makeQuery(id+"F2.opExtrude","SWEPT_BODY",BODY,{"disambiguationData":[OSD([sQuery(id+"F0.wireOp",EDGE,"E94"),sQuery(id+"F0.wireOp",EDGE,"E95"),sQuery(id+"F0.wireOp",EDGE,"E96"),sQuery(id+"F0.wireOp",EDGE,"E97")])]});
            var Q26;
            Q26=makeQuery(id+"F2.opExtrude","SWEPT_BODY",BODY,{"disambiguationData":[OSD([sQuery(id+"F0.wireOp",EDGE,"E99"),sQuery(id+"F0.wireOp",EDGE,"E100"),sQuery(id+"F0.wireOp",EDGE,"E101"),sQuery(id+"F0.wireOp",EDGE,"E102")])]});
            var Q27;
            Q27=makeQuery(id+"F2.opExtrude","SWEPT_BODY",BODY,{"disambiguationData":[OSD([sQuery(id+"F0.wireOp",EDGE,"E104"),sQuery(id+"F0.wireOp",EDGE,"E105"),sQuery(id+"F0.wireOp",EDGE,"E106"),sQuery(id+"F0.wireOp",EDGE,"E107")])]});
            var Q28;
            Q28=makeQuery(id+"F2.opExtrude","SWEPT_BODY",BODY,{"disambiguationData":[OSD([sQuery(id+"F0.wireOp",EDGE,"E124"),sQuery(id+"F0.wireOp",EDGE,"E125"),sQuery(id+"F0.wireOp",EDGE,"E126"),sQuery(id+"F0.wireOp",EDGE,"E127")])]});
            var Q29;
            Q29=makeQuery(id+"F2.opExtrude","SWEPT_BODY",BODY,{"disambiguationData":[OSD([sQuery(id+"F0.wireOp",EDGE,"E114"),sQuery(id+"F0.wireOp",EDGE,"E115"),sQuery(id+"F0.wireOp",EDGE,"E116"),sQuery(id+"F0.wireOp",EDGE,"E117")])]});
            var Q30;
            Q30=makeQuery(id+"F2.opExtrude","SWEPT_BODY",BODY,{"disambiguationData":[OSD([sQuery(id+"F0.wireOp",EDGE,"E119"),sQuery(id+"F0.wireOp",EDGE,"E120"),sQuery(id+"F0.wireOp",EDGE,"E121"),sQuery(id+"F0.wireOp",EDGE,"E122")])]});
            booleanBodies(context, id + "F5", {"operationType" : BooleanOperationType.SUBTRACTION, "tools" : qUnion([Q0]), "targets" : qUnion([Q1, Q2, Q3, Q4, Q5, Q6, Q7, Q8, Q9, Q10, Q11, Q12, Q13, Q14, Q15, Q16, Q17, Q18, Q19, Q20, Q21, Q22, Q23, Q24, Q25, Q26, Q27, Q28, Q29, Q30])});
        }
    });
